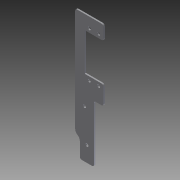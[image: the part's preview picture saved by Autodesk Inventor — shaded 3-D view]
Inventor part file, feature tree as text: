
AUTODESK INVENTOR PART (.ipt)
format: ipt  version: 2012 (Build 160160000, 160)  size: 178,176 bytes
history: native  units: mm
features: sketch x2, extrude x1, plane x1, hole x1
ambient origin geometry x8: Origin, YZ Plane, XZ Plane, XY Plane, X Axis, Y Axis, Z Axis, Center Point
feature tree (5):
  extrude  "Extrusion2"  Depth=10.0mm
  plane  "Work Plane1"
  hole  "Hole1"  [1 undecoded]
  sketch  "Sketch1"  dims[d0=5.0mm d1=20.0mm d2=3.0mm d3=5.0mm d4=4.0mm d5=3.0mm d6=10.0mm d7=3.0mm d8=3.0mm d9=10.0mm d10=5.0mm d11=4.0mm d14=15.0mm d15=135.75mm d18=10.0mm]
  sketch  "Sketch4"  dims[d19=15.0mm d21=30.0mm d22=2.0mm d23=5.0mm d26=3.0mm d27=3.0mm d29=30.0mm d30=1.5mm d31=0.0mm d32=0.0mm d33=5.0mm d34=20.0mm d35=3.0mm d36=5.0mm d37=4.0mm d38=3.0mm d39=10.0mm d40=3.0mm d41=3.0mm d42=10.0mm d43=5.0mm d44=4.0mm d45=15.0mm d46=135.75mm d47=10.0mm d48=15.0mm d49=30.0mm d50=2.0mm d51=5.0mm d52=3.0mm d53=3.0mm d54=30.0mm d55=3.0mm d56=6.0mm d57=4.0mm d58=2.0mm d59=90.0deg d60=8.0mm d61=20.594885mm d62=48.0mm d63=48.0mm]
note: 1 required parameter value undecoded (feature->parameter linkage not recoverable at this tier; creation-order binding heuristic only, values carry confidence <= 0.55)
